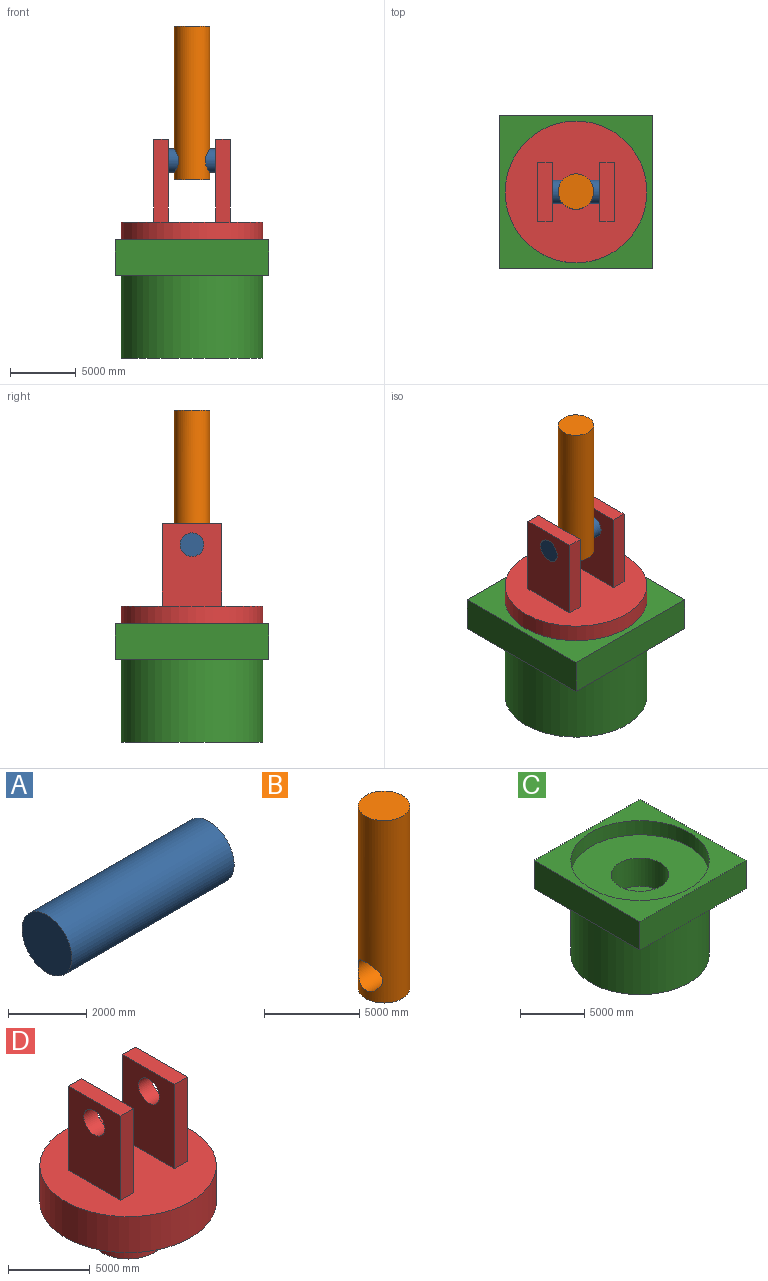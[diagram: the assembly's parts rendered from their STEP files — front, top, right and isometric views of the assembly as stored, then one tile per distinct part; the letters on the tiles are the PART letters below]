
ASSEMBLY  parts=4 mates=3
PART A: 3 faces, bbox 5850x1800x1800 mm
  f0: plane 1800x1800mm, normal (-1,0,0), area 2544690mm2, adj f1
  f1: cylinder r=900mm len=5850mm, axis (1,0,0), area 33080970.6mm2, adj f0,f2
  f2: plane 1800x1800mm, normal (1,0,0), area 2544690mm2, adj f1
PART B: 4 faces, bbox 2700x2700x11700 mm
  f0: cylinder r=1350mm len=11700mm, axis (0,0,-1), area 93812789.2mm2, adj f1,f2,f3
  f1: plane 2700x2700mm, normal (0,0,1), area 5725552.6mm2, adj f0
  f2: plane 2700x2700mm, normal (0,0,-1), area 5725552.6mm2, adj f0
  f3: cylinder r=900mm len=2700.01mm, axis (1,0,0), area 13393440.8mm2, adj f0
PART C: 12 faces, bbox 11700x11700x9000 mm
  f0: plane 11700x2700mm, normal (1,0,0), area 31590000mm2, adj f1,f3,f4,f5
  f1: plane 11700x2700mm, normal (0,1,0), area 31590000mm2, adj f0,f2,f4,f5
  f2: plane 11700x2700mm, normal (-1,0,0), area 31590000mm2, adj f1,f3,f4,f5
  f3: plane 11700x2700mm, normal (0,-1,0), area 31590000mm2, adj f0,f2,f4,f5
  f4: plane 11700x11700mm, normal (0,0,1), area 45281158.2mm2, adj f0,f1,f2,f3,f8
  f5: plane 11700x11700mm, normal (0,0,-1), area 45281158.2mm2, adj f0,f1,f2,f3,f6
  f6: cylinder r=5400mm len=10800mm, axis (0,0,1), area 213753964.2mm2, adj f5,f7
  f7: plane 10800x10800mm, normal (0,0,-1), area 91608841.8mm2, adj f6
  f8: cylinder r=5400mm len=10800mm, axis (0,0,-1), area 45804420.9mm2, adj f4,f9
  f9: plane 10800x10800mm, normal (0,0,1), area 75704529mm2, adj f8,f10
  f10: cylinder r=2250mm len=4500mm, axis (0,0,1), area 38170350.7mm2, adj f9,f11
  f11: plane 4500x4500mm, normal (0,0,1), area 15904312.8mm2, adj f10
PART D: 17 faces, bbox 10800x10800x11700 mm
  f0: plane 10800x10800mm, normal (0,0,1), area 81483841.8mm2, adj f1,f3,f4,f5,f6,f8,f9,f10
  f1: cylinder r=5400mm len=10800mm, axis (0,0,-1), area 91608841.8mm2, adj f0,f2
  f2: plane 10800x10800mm, normal (0,0,-1), area 75704529mm2, adj f1,f13
  f3: plane 6300x4500mm, normal (-1,0,0), area 25805310mm2, adj f0,f4,f6,f7,f16
  f4: plane 6300x1125mm, normal (0,-1,0), area 7087500mm2, adj f0,f3,f5,f7
  f5: plane 6300x4500mm, normal (1,0,0), area 25805310mm2, adj f0,f4,f6,f7,f16
  f6: plane 6300x1125mm, normal (0,1,0), area 7087500mm2, adj f0,f3,f5,f7
  f7: plane 4500x1125mm, normal (0,0,1), area 5062500mm2, adj f3,f4,f5,f6
  f8: plane 6300x1125mm, normal (0,1,0), area 7087500mm2, adj f0,f9,f11,f12
  f9: plane 6300x4500mm, normal (-1,0,0), area 25805310mm2, adj f0,f8,f10,f12,f15
  f10: plane 6300x1125mm, normal (0,-1,0), area 7087500mm2, adj f0,f9,f11,f12
  f11: plane 6300x4500mm, normal (1,0,0), area 25805310mm2, adj f0,f8,f10,f12,f15
  f12: plane 4500x1125mm, normal (0,0,1), area 5062500mm2, adj f8,f9,f10,f11
  f13: cylinder r=2250mm len=4500mm, axis (0,0,1), area 38170350.7mm2, adj f2,f14
  f14: plane 4500x4500mm, normal (0,0,-1), area 15904312.8mm2, adj f13
  f15: cylinder r=900mm len=1800mm, axis (1,0,0), area 6361725.1mm2, adj f9,f11
  f16: cylinder r=900mm len=1800mm, axis (1,0,0), area 6361725.1mm2, adj f3,f5
PLACE A rot(axis=(-0.07,-0.34,-0.94),0deg) t=(0,0,0)mm
PLACE B rot(axis=(-0.29,-0.5,-0.82),0deg) t=(-0.07,0,0)mm
PLACE C at identity fixed
PLACE D at identity
MATE revolute D.f1 <-> C.f6  axis (0,0,-1) through (0,0,-1350)mm
MATE fastened B.f3 <-> A.f1  axis (1,0,0) through (0,0,8730)mm
MATE revolute A.f1 <-> D.f15  axis (1,0,0) through (2925,0,8730)mm
